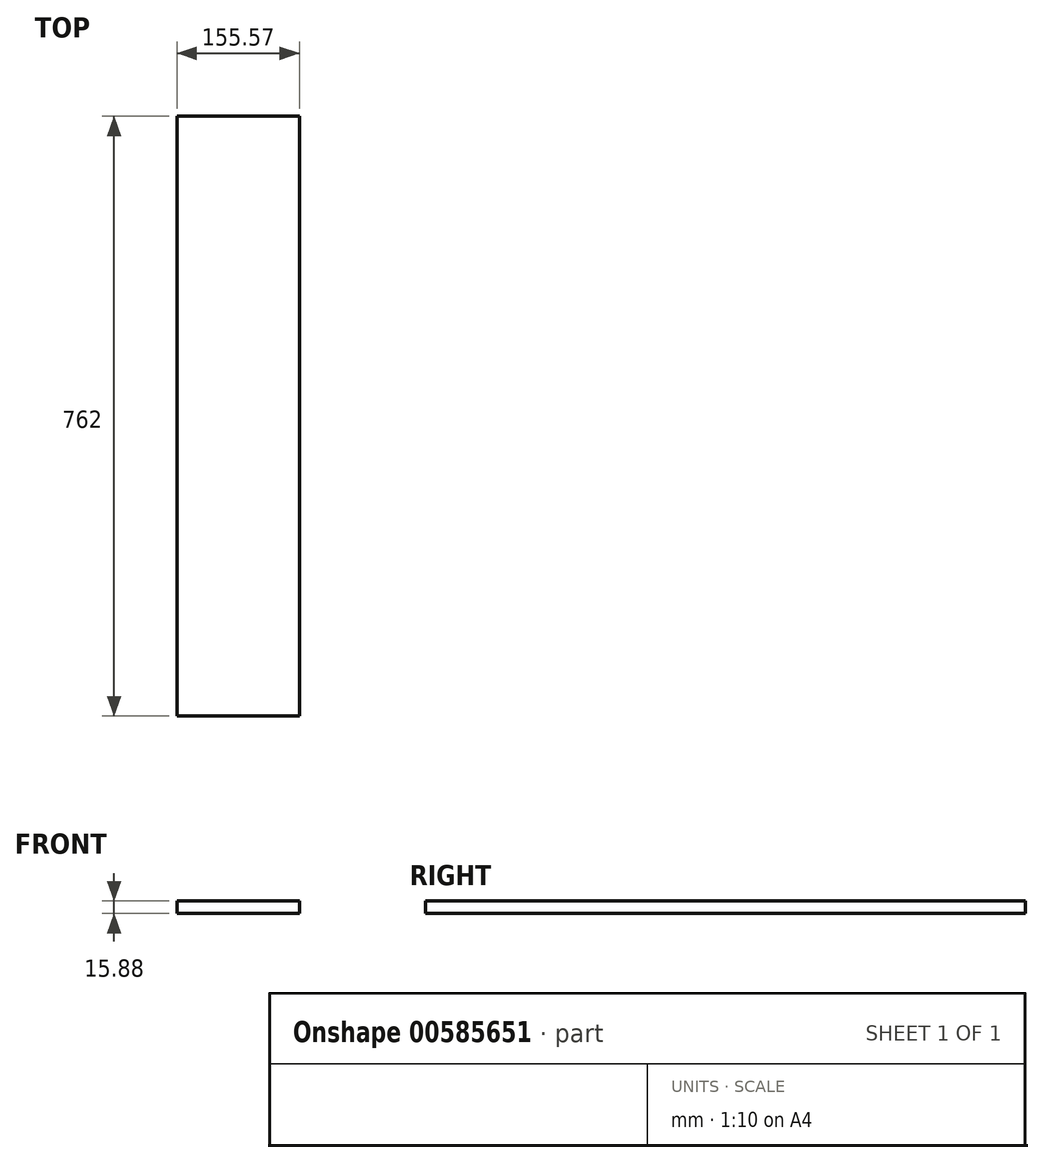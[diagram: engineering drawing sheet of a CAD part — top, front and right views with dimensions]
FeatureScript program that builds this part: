
annotation { "Feature Type Name" : "Feature", "Feature Type Description" : "" }
export const myFeature = defineFeature(function(context is Context, id is Id, definition is map)
    precondition{}
    {
        {
            var Q0;
            Q0=qCreatedBy(makeId("Front.planeOp"),FACE);
            var sketch = newSketch(context, id + "F0", { "sketchPlane" : qUnion([Q0])});
            skLineSegment(sketch, "E0.bottom", {"start": v(0, 0) * mm, "end": v(155.58, 0) * mm});
            skLineSegment(sketch, "E0.top", {"start": v(0, 15.88) * mm, "end": v(155.58, 15.88) * mm});
            skLineSegment(sketch, "E0.left", {"start": v(0, 0) * mm, "end": v(0, 15.88) * mm});
            skLineSegment(sketch, "E0.right", {"start": v(155.58, 0) * mm, "end": v(155.58, 15.88) * mm});
            skSolve(sketch);
        }
        {
            var Q0;
            Q0=makeQuery(id+"F0.imprint","IMPRINT",FACE,{"disambiguationData":[TD([[makeQuery(id+"F0.imprint","IMPRINT",EDGE,{"derivedFrom":sQuery(id+"F0.wireOp",EDGE,"E0.bottom")}),1.0]])]});
            extrude(context, id + "F1", {"entities" : qUnion([Q0]), "oppositeDirection" : true, "depth" : 762 * mm, "offsetDistance" : 25.4 * mm});
        }
    });
